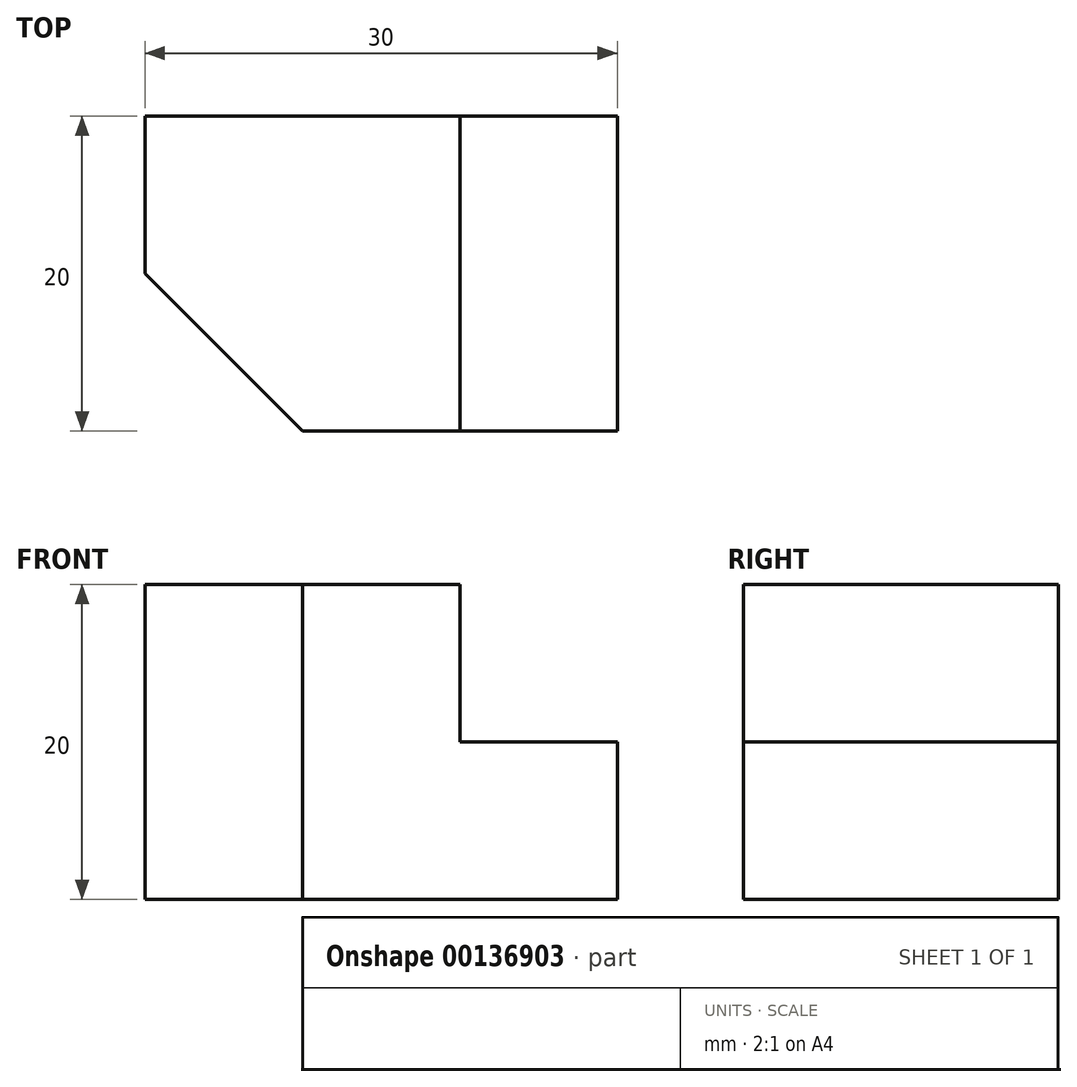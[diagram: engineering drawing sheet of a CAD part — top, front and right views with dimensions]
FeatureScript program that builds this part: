
annotation { "Feature Type Name" : "Feature", "Feature Type Description" : "" }
export const myFeature = defineFeature(function(context is Context, id is Id, definition is map)
    precondition{}
    {
        {
            var Q0;
            Q0=qCreatedBy(makeId("Top.planeOp"),FACE);
            var sketch = newSketch(context, id + "F0", { "sketchPlane" : qUnion([Q0])});
            skLineSegment(sketch, "E0", {"start": v(0, 0) * mm, "end": v(0, 10) * mm});
            skLineSegment(sketch, "E1", {"start": v(0, 10) * mm, "end": v(30, 10) * mm});
            skLineSegment(sketch, "E2", {"start": v(30, 10) * mm, "end": v(30, -10) * mm});
            skLineSegment(sketch, "E3", {"start": v(30, -10) * mm, "end": v(10, -10) * mm});
            skLineSegment(sketch, "E4", {"start": v(10, -10) * mm, "end": v(0, 0) * mm});
            skSolve(sketch);
        }
        {
            var Q0;
            Q0 = qSketchRegion(id + "F0", true);
            extrude(context, id + "F1", {"entities" : qUnion([Q0]), "depth" : 20 * mm});
        }
        {
            var Q0;
            Q0=makeQuery(id+"F1.opExtrude","SWEPT_FACE",FACE,{"disambiguationData":[OSD([sQuery(id+"F0.wireOp",EDGE,"E3")])]});
            var sketch = newSketch(context, id + "F2", { "sketchPlane" : qUnion([Q0])});
            skLineSegment(sketch, "E5", {"start": v(30, 10) * mm, "end": v(20, 10) * mm});
            skLineSegment(sketch, "E6", {"start": v(20, 10) * mm, "end": v(20, 20) * mm});
            skLineSegment(sketch, "E7", {"start": v(20, 20) * mm, "end": v(30, 20) * mm});
            skLineSegment(sketch, "E8", {"start": v(30, 20) * mm, "end": v(30, 10) * mm});
            skSolve(sketch);
        }
        {
            var Q0;
            Q0 = qSketchRegion(id + "F2", true);
            extrude(context, id + "F3", {"entities" : qUnion([Q0]), "operationType" : NewBodyOperationType.REMOVE, "oppositeDirection" : true, "depth" : 25 * mm});
        }
    });
